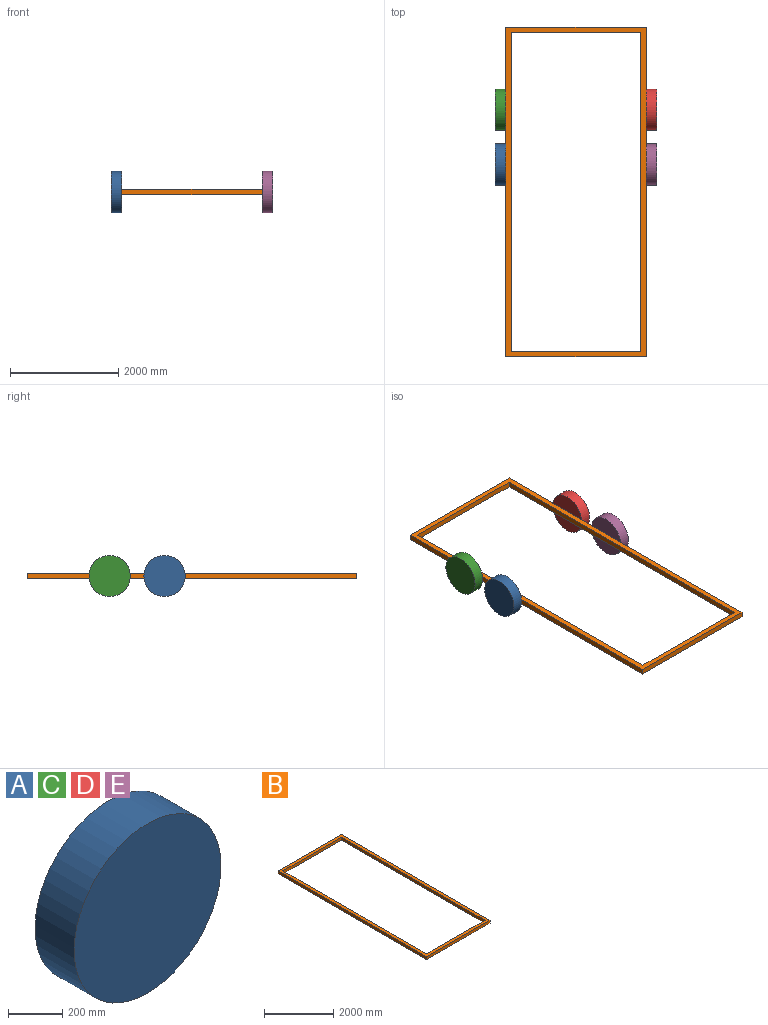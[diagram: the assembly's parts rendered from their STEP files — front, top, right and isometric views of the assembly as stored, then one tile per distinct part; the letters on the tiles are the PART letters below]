
ASSEMBLY  parts=5 mates=4
PART A: 3 faces, bbox 762x203.2x762 mm
  f0: cylinder r=381mm len=762mm, axis (0,1,0), area 486439.2mm2, adj f1,f2
  f1: plane 762x762mm, normal (0,-1,0), area 456036.7mm2, adj f0
  f2: plane 762x762mm, normal (0,1,0), area 456036.7mm2, adj f0
PART B: 10 faces, bbox 2590.8x6096x101.6 mm
  f0: plane 2590.8x101.6mm, normal (0,1,0), area 263225.3mm2, adj f1,f7,f8,f9
  f1: plane 6096x101.6mm, normal (-1,0,0), area 619353.6mm2, adj f0,f2,f8,f9
  f2: plane 2590.8x101.6mm, normal (0,-1,0), area 263225.3mm2, adj f1,f7,f8,f9
  f3: plane 5892.8x101.6mm, normal (1,0,0), area 598708.5mm2, adj f4,f6,f8,f9
  f4: plane 2387.6x101.6mm, normal (0,-1,0), area 242580.2mm2, adj f3,f5,f8,f9
  f5: plane 5892.8x101.6mm, normal (-1,0,0), area 598708.5mm2, adj f4,f6,f8,f9
  f6: plane 2387.6x101.6mm, normal (0,1,0), area 242580.2mm2, adj f3,f5,f8,f9
  f7: plane 6096x101.6mm, normal (1,0,0), area 619353.6mm2, adj f0,f2,f8,f9
  f8: plane 6096x2590.8mm, normal (0,0,1), area 1723867.5mm2, adj f0,f1,f2,f3,f4,f5,f6,f7
  f9: plane 6096x2590.8mm, normal (0,0,-1), area 1723867.5mm2, adj f0,f1,f2,f3,f4,f5,f6,f7
PART C: same geometry as A
PART D: same geometry as A
PART E: same geometry as A
PLACE A rot(axis=(0.71,0.71,0),180deg) t=(-1295.4,508,0)mm
PLACE B t=(-1295.4,-3048,-50.8)mm fixed
PLACE C rot(axis=(0,0,-1),90deg) t=(-1295.4,1524,0)mm
PLACE D rot(axis=(0.71,0.71,0),180deg) t=(1498.6,1524,0)mm
PLACE E rot(axis=(0,0,1),90deg) t=(1295.4,508,0)mm
MATE fastened C.f0 <-> B.f1  axis (1,0,0) through (-1295.4,1524,0)mm
MATE fastened E.f0 <-> B.f7  axis (-1,0,0) through (1295.4,508,0)mm
MATE fastened D.f0 <-> B.f7  axis (-1,0,0) through (1295.4,1524,0)mm
MATE fastened A.f0 <-> B.f1  axis (1,0,0) through (-1295.4,508,0)mm
